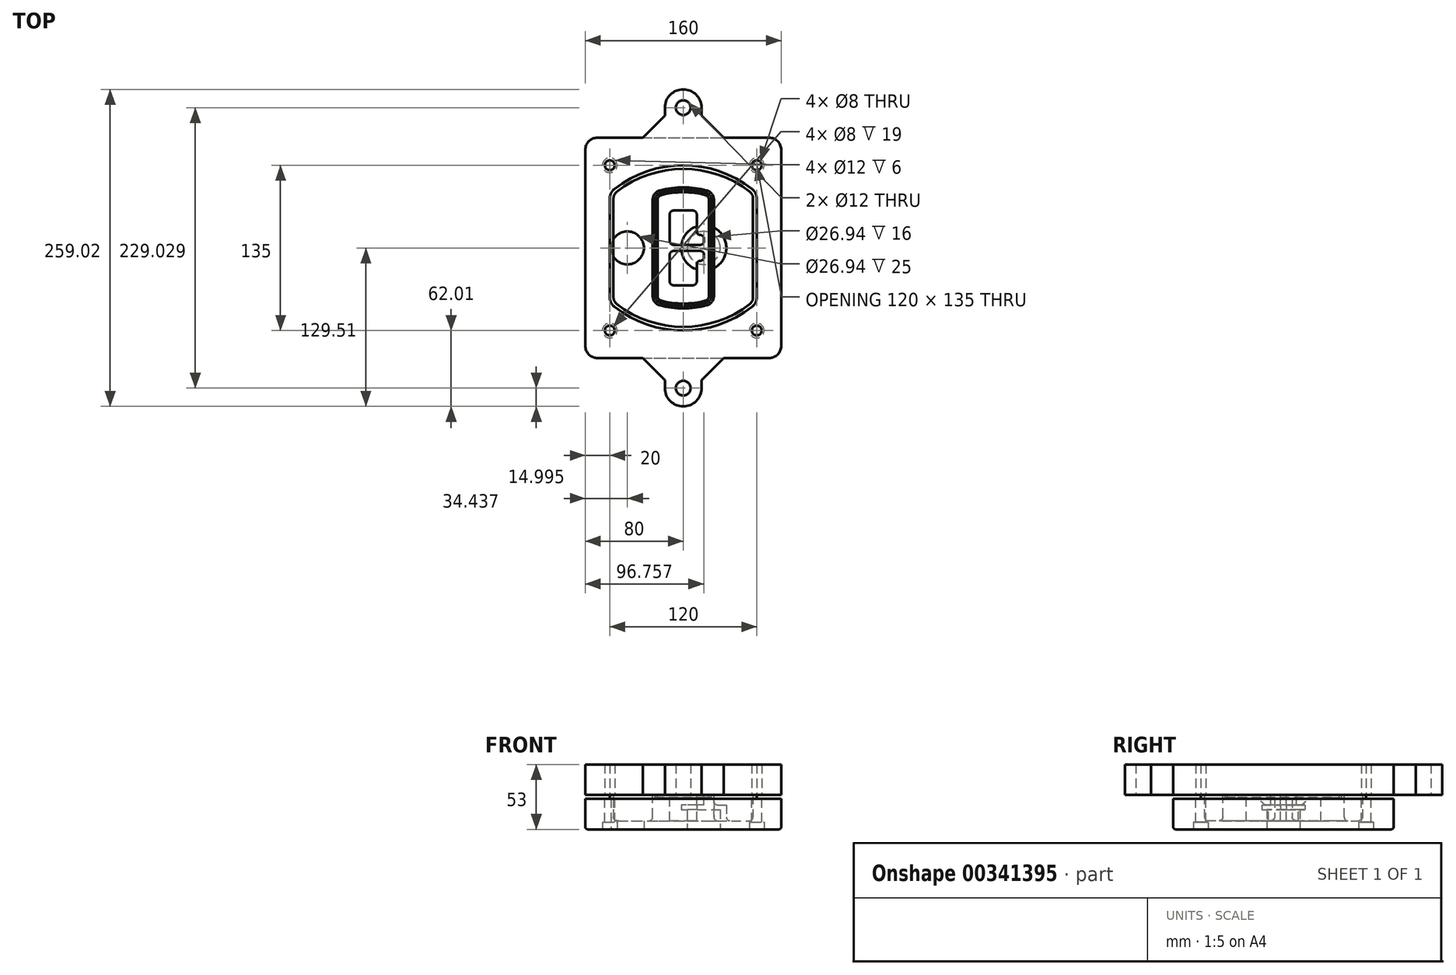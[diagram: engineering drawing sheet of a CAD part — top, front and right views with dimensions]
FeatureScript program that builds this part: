
annotation { "Feature Type Name" : "Feature", "Feature Type Description" : "" }
export const myFeature = defineFeature(function(context is Context, id is Id, definition is map)
    precondition{}
    {
        {
            var Q0;
            Q0=qCreatedBy(makeId("Top.planeOp"),FACE);
            var sketch = newSketch(context, id + "F0", { "sketchPlane" : qUnion([Q0])});
            skPoint(sketch, "E0.rect.middle", {"position": v(0, 0) * mm});
            skLineSegment(sketch, "E1.bottom", {"start": v(-70, -90) * mm, "end": v(70, -90) * mm});
            skLineSegment(sketch, "E1.top", {"start": v(-70, 90) * mm, "end": v(70, 90) * mm});
            skLineSegment(sketch, "E1.left", {"start": v(-80, -80) * mm, "end": v(-80, 80) * mm});
            skLineSegment(sketch, "E1.right", {"start": v(80, -80) * mm, "end": v(80, 80) * mm});
            skLineSegment(sketch, "E2", {"start": v(-80, 90) * mm, "end": v(80, -90) * mm, "construction": true});
            skLineSegment(sketch, "E3", {"start": v(80, 90) * mm, "end": v(-80, -90) * mm, "construction": true});
            skCircle(sketch, "E4", {"center": v(-60, 67.5) * mm, "radius": 4 * mm});
            skCircle(sketch, "E5", {"center": v(60, 67.5) * mm, "radius": 4 * mm});
            skCircle(sketch, "E6", {"center": v(60, -67.5) * mm, "radius": 4 * mm});
            skCircle(sketch, "E7", {"center": v(-60, -67.5) * mm, "radius": 4 * mm});
            skLineSegment(sketch, "E8", {"start": v(-60, 67.5) * mm, "end": v(60, 67.5) * mm, "construction": true});
            skLineSegment(sketch, "E9", {"start": v(60, 67.5) * mm, "end": v(60, -67.5) * mm, "construction": true});
            skLineSegment(sketch, "E10", {"start": v(60, -67.5) * mm, "end": v(-60, -67.5) * mm, "construction": true});
            skLineSegment(sketch, "E11", {"start": v(-60, -67.5) * mm, "end": v(-60, 67.5) * mm, "construction": true});
            skLineSegment(sketch, "E12", {"start": v(-60, 40.3) * mm, "end": v(-60, -40.3) * mm});
            skLineSegment(sketch, "E13", {"start": v(60, 40.3) * mm, "end": v(60, -40.3) * mm});
            skArc(sketch, "E14", {"start": v(56.15, 48.18) * mm, "mid": v(0, 67.5) * mm, "end": v(-56.15, 48.18) * mm});
            skArc(sketch, "E15", {"start": v(-56.15, -48.18) * mm, "mid": v(0, -67.5) * mm, "end": v(56.15, -48.18) * mm});
            skLineSegment(sketch, "E16", {"start": v(-60, 0) * mm, "end": v(60, 0) * mm, "construction": true});
            skPoint(sketch, "E17.visualSharp", {"position": v(-60, -45) * mm});
            skArc(sketch, "E17.filletArc", {"start": v(-60, -40.3) * mm, "mid": v(-58.99, -44.68) * mm, "end": v(-56.15, -48.18) * mm});
            skPoint(sketch, "E18.visualSharp", {"position": v(-60, 45) * mm});
            skArc(sketch, "E18.filletArc", {"start": v(-56.15, 48.18) * mm, "mid": v(-58.99, 44.68) * mm, "end": v(-60, 40.3) * mm});
            skPoint(sketch, "E19.visualSharp", {"position": v(60, 45) * mm});
            skArc(sketch, "E19.filletArc", {"start": v(60, 40.3) * mm, "mid": v(58.99, 44.68) * mm, "end": v(56.15, 48.18) * mm});
            skPoint(sketch, "E20.visualSharp", {"position": v(60, -45) * mm});
            skArc(sketch, "E20.filletArc", {"start": v(56.15, -48.18) * mm, "mid": v(58.99, -44.68) * mm, "end": v(60, -40.3) * mm});
            skPoint(sketch, "E21.visualSharp", {"position": v(-80, 90) * mm});
            skArc(sketch, "E21.filletArc", {"start": v(-70, 90) * mm, "mid": v(-77.07, 87.07) * mm, "end": v(-80, 80) * mm});
            skPoint(sketch, "E22.visualSharp", {"position": v(80, 90) * mm});
            skArc(sketch, "E22.filletArc", {"start": v(80, 80) * mm, "mid": v(77.07, 87.07) * mm, "end": v(70, 90) * mm});
            skPoint(sketch, "E23.visualSharp", {"position": v(80, -90) * mm});
            skArc(sketch, "E23.filletArc", {"start": v(70, -90) * mm, "mid": v(77.07, -87.07) * mm, "end": v(80, -80) * mm});
            skPoint(sketch, "E24.visualSharp", {"position": v(-80, -90) * mm});
            skArc(sketch, "E24.filletArc", {"start": v(-80, -80) * mm, "mid": v(-77.07, -87.07) * mm, "end": v(-70, -90) * mm});
            skArc(sketch, "E25.0", {"start": v(57, 40.3) * mm, "mid": v(56.3, 43.36) * mm, "end": v(54.3, 45.81) * mm});
            skLineSegment(sketch, "E25.1", {"start": v(57, 40.3) * mm, "end": v(57, -40.3) * mm});
            skArc(sketch, "E25.2", {"start": v(54.3, -45.81) * mm, "mid": v(56.3, -43.36) * mm, "end": v(57, -40.3) * mm});
            skArc(sketch, "E25.3", {"start": v(-54.3, -45.81) * mm, "mid": v(0, -64.5) * mm, "end": v(54.3, -45.81) * mm});
            skArc(sketch, "E25.4", {"start": v(-57, -40.3) * mm, "mid": v(-56.3, -43.36) * mm, "end": v(-54.3, -45.81) * mm});
            skArc(sketch, "E25.5", {"start": v(54.3, 45.81) * mm, "mid": v(0, 64.5) * mm, "end": v(-54.3, 45.81) * mm});
            skLineSegment(sketch, "E25.6", {"start": v(-57, 40.3) * mm, "end": v(-57, -40.3) * mm});
            skArc(sketch, "E25.7", {"start": v(-54.3, 45.81) * mm, "mid": v(-56.3, 43.36) * mm, "end": v(-57, 40.3) * mm});
            skArc(sketch, "E26.0", {"start": v(-58.62, 51.33) * mm, "mid": v(-62.58, 46.43) * mm, "end": v(-64, 40.3) * mm});
            skArc(sketch, "E26.1", {"start": v(58.62, 51.33) * mm, "mid": v(0, 71.5) * mm, "end": v(-58.62, 51.33) * mm});
            skArc(sketch, "E26.2", {"start": v(64, 40.3) * mm, "mid": v(62.58, 46.43) * mm, "end": v(58.62, 51.33) * mm});
            skLineSegment(sketch, "E26.3", {"start": v(64, 40.3) * mm, "end": v(64, -40.3) * mm});
            skArc(sketch, "E26.4", {"start": v(58.62, -51.33) * mm, "mid": v(62.58, -46.43) * mm, "end": v(64, -40.3) * mm});
            skLineSegment(sketch, "E26.5", {"start": v(-64, 40.3) * mm, "end": v(-64, -40.3) * mm});
            skArc(sketch, "E26.6", {"start": v(-58.62, -51.33) * mm, "mid": v(0, -71.5) * mm, "end": v(58.62, -51.33) * mm});
            skArc(sketch, "E26.7", {"start": v(-64, -40.3) * mm, "mid": v(-62.58, -46.43) * mm, "end": v(-58.62, -51.33) * mm});
            skSolve(sketch);
        }
        {
            var Q0;
            Q0=makeQuery(id+"F0.imprint","IMPRINT",FACE,{"disambiguationData":[TD([[makeQuery(id+"F0.imprint","IMPRINT",EDGE,{"derivedFrom":sQuery(id+"F0.wireOp",EDGE,"E1.bottom")}),1.0]])]});
            var Q1;
            Q1=makeQuery(id+"F0.imprint","IMPRINT",FACE,{"disambiguationData":[TD([[makeQuery(id+"F0.imprint","IMPRINT",EDGE,{"derivedFrom":sQuery(id+"F0.wireOp",EDGE,"E12")}),1.0]])]});
            var Q2;
            Q2=makeQuery(id+"F0.imprint","IMPRINT",FACE,{"disambiguationData":[TD([[makeQuery(id+"F0.imprint","IMPRINT",EDGE,{"derivedFrom":sQuery(id+"F0.wireOp",EDGE,"E25.0")}),1.0]])]});
            var Q3;
            Q3=makeQuery(id+"F0.imprint","IMPRINT",FACE,{"disambiguationData":[TD([[makeQuery(id+"F0.imprint","IMPRINT",EDGE,{"derivedFrom":sQuery(id+"F0.wireOp",EDGE,"E12")}),-1.0]])]});
            extrude(context, id + "F1", {"entities" : qUnion([Q0, Q1, Q2, Q3]), "oppositeDirection" : true, "depth" : 25 * mm});
        }
        {
            var Q0;
            Q0=makeQuery(id+"F0.imprint","IMPRINT",FACE,{"disambiguationData":[TD([[makeQuery(id+"F0.imprint","IMPRINT",EDGE,{"derivedFrom":sQuery(id+"F0.wireOp",EDGE,"E12")}),1.0]])]});
            extrude(context, id + "F2", {"entities" : qUnion([Q0]), "operationType" : NewBodyOperationType.ADD, "depth" : 3 * mm});
        }
        {
            var Q0;
            Q0=makeQuery(id+"F0.imprint","IMPRINT",FACE,{"disambiguationData":[TD([[makeQuery(id+"F0.imprint","IMPRINT",EDGE,{"derivedFrom":sQuery(id+"F0.wireOp",EDGE,"E25.0")}),1.0]])]});
            extrude(context, id + "F3", {"entities" : qUnion([Q0]), "operationType" : NewBodyOperationType.REMOVE, "oppositeDirection" : true, "depth" : 18 * mm});
        }
        {
            var Q0;
            Q0=makeQuery(id+"F2.opExtrude","CAP_FACE",FACE,{"disambiguationData":[OSD([sQuery(id+"F0.wireOp",EDGE,"E12"),sQuery(id+"F0.wireOp",EDGE,"E13"),sQuery(id+"F0.wireOp",EDGE,"E14"),sQuery(id+"F0.wireOp",EDGE,"E15"),sQuery(id+"F0.wireOp",EDGE,"E17.filletArc"),sQuery(id+"F0.wireOp",EDGE,"E18.filletArc"),sQuery(id+"F0.wireOp",EDGE,"E19.filletArc"),sQuery(id+"F0.wireOp",EDGE,"E20.filletArc"),sQuery(id+"F0.wireOp",EDGE,"E25.0"),sQuery(id+"F0.wireOp",EDGE,"E25.1"),sQuery(id+"F0.wireOp",EDGE,"E25.2"),sQuery(id+"F0.wireOp",EDGE,"E25.3"),sQuery(id+"F0.wireOp",EDGE,"E25.4"),sQuery(id+"F0.wireOp",EDGE,"E25.5"),sQuery(id+"F0.wireOp",EDGE,"E25.6"),sQuery(id+"F0.wireOp",EDGE,"E25.7")])],"isStart":false});
            var sketch = newSketch(context, id + "F4", { "sketchPlane" : qUnion([Q0])});
            skArc(sketch, "E27.0", {"start": v(-19.08, -46.97) * mm, "mid": v(0, -49.5) * mm, "end": v(19.08, -46.97) * mm});
            skArc(sketch, "E28.0", {"start": v(19.08, 46.97) * mm, "mid": v(0, 49.5) * mm, "end": v(-19.08, 46.97) * mm});
            skLineSegment(sketch, "E29", {"start": v(-25, 39.25) * mm, "end": v(-25, -39.25) * mm});
            skLineSegment(sketch, "E30", {"start": v(25, 39.25) * mm, "end": v(25, -39.25) * mm});
            skLineSegment(sketch, "E31", {"start": v(-25, 45.1) * mm, "end": v(25, 45.1) * mm, "construction": true});
            skLineSegment(sketch, "E32", {"start": v(-25, -45.1) * mm, "end": v(25, -45.1) * mm, "construction": true});
            skPoint(sketch, "E33.visualSharp", {"position": v(-25, 45.1) * mm});
            skArc(sketch, "E33.filletArc", {"start": v(-19.08, 46.97) * mm, "mid": v(-23.35, 44.11) * mm, "end": v(-25, 39.25) * mm});
            skPoint(sketch, "E34.visualSharp", {"position": v(25, 45.1) * mm});
            skArc(sketch, "E34.filletArc", {"start": v(25, 39.25) * mm, "mid": v(23.35, 44.11) * mm, "end": v(19.08, 46.97) * mm});
            skPoint(sketch, "E35.visualSharp", {"position": v(25, -45.1) * mm});
            skArc(sketch, "E35.filletArc", {"start": v(19.08, -46.97) * mm, "mid": v(23.35, -44.11) * mm, "end": v(25, -39.25) * mm});
            skPoint(sketch, "E36.visualSharp", {"position": v(-25, -45.1) * mm});
            skArc(sketch, "E36.filletArc", {"start": v(-25, -39.25) * mm, "mid": v(-23.35, -44.11) * mm, "end": v(-19.08, -46.97) * mm});
            skArc(sketch, "E37.0", {"start": v(54.3, 45.81) * mm, "mid": v(0, 64.5) * mm, "end": v(-54.3, 45.81) * mm});
            skArc(sketch, "E37.1", {"start": v(-54.3, 45.81) * mm, "mid": v(-56.3, 43.36) * mm, "end": v(-57, 40.3) * mm});
            skLineSegment(sketch, "E37.2", {"start": v(-57, 40.3) * mm, "end": v(-57, -40.3) * mm});
            skArc(sketch, "E37.3", {"start": v(-57, -40.3) * mm, "mid": v(-56.3, -43.36) * mm, "end": v(-54.3, -45.81) * mm});
            skArc(sketch, "E37.4", {"start": v(-54.3, -45.81) * mm, "mid": v(0, -64.5) * mm, "end": v(54.3, -45.81) * mm});
            skArc(sketch, "E37.5", {"start": v(54.3, -45.81) * mm, "mid": v(56.3, -43.36) * mm, "end": v(57, -40.3) * mm});
            skLineSegment(sketch, "E37.6", {"start": v(57, 40.3) * mm, "end": v(57, -40.3) * mm});
            skArc(sketch, "E37.7", {"start": v(57, 40.3) * mm, "mid": v(56.3, 43.36) * mm, "end": v(54.3, 45.81) * mm});
            skLineSegment(sketch, "E38.0", {"start": v(23, 39.25) * mm, "end": v(23, -39.25) * mm});
            skArc(sketch, "E38.1", {"start": v(18.56, -45.04) * mm, "mid": v(21.76, -42.9) * mm, "end": v(23, -39.25) * mm});
            skArc(sketch, "E38.2", {"start": v(-18.56, -45.04) * mm, "mid": v(0, -47.5) * mm, "end": v(18.56, -45.04) * mm});
            skArc(sketch, "E38.3", {"start": v(-23, -39.25) * mm, "mid": v(-21.76, -42.9) * mm, "end": v(-18.56, -45.04) * mm});
            skLineSegment(sketch, "E38.4", {"start": v(-23, 39.25) * mm, "end": v(-23, -39.25) * mm});
            skArc(sketch, "E38.5", {"start": v(23, 39.25) * mm, "mid": v(21.76, 42.9) * mm, "end": v(18.56, 45.04) * mm});
            skArc(sketch, "E38.6", {"start": v(-18.56, 45.04) * mm, "mid": v(-21.76, 42.9) * mm, "end": v(-23, 39.25) * mm});
            skArc(sketch, "E38.7", {"start": v(18.56, 45.04) * mm, "mid": v(0, 47.5) * mm, "end": v(-18.56, 45.04) * mm});
            skArc(sketch, "E39.0", {"start": v(21, 39.25) * mm, "mid": v(20.18, 41.68) * mm, "end": v(18.04, 43.1) * mm});
            skLineSegment(sketch, "E39.1", {"start": v(21, 39.25) * mm, "end": v(21, -39.25) * mm});
            skArc(sketch, "E39.2", {"start": v(18.04, -43.1) * mm, "mid": v(20.18, -41.68) * mm, "end": v(21, -39.25) * mm});
            skArc(sketch, "E39.3", {"start": v(-18.04, -43.1) * mm, "mid": v(0, -45.5) * mm, "end": v(18.04, -43.1) * mm});
            skArc(sketch, "E39.4", {"start": v(-21, -39.25) * mm, "mid": v(-20.18, -41.68) * mm, "end": v(-18.04, -43.1) * mm});
            skArc(sketch, "E39.5", {"start": v(18.04, 43.1) * mm, "mid": v(0, 45.5) * mm, "end": v(-18.04, 43.1) * mm});
            skLineSegment(sketch, "E39.6", {"start": v(-21, 39.25) * mm, "end": v(-21, -39.25) * mm});
            skArc(sketch, "E39.7", {"start": v(-18.04, 43.1) * mm, "mid": v(-20.18, 41.68) * mm, "end": v(-21, 39.25) * mm});
            skLineSegment(sketch, "E40", {"start": v(-25, 0) * mm, "end": v(25, 0) * mm, "construction": true});
            skLineSegment(sketch, "E41", {"start": v(-11, 5.5) * mm, "end": v(-11, 27.5) * mm});
            skLineSegment(sketch, "E42", {"start": v(-8, 30.5) * mm, "end": v(8, 30.5) * mm});
            skLineSegment(sketch, "E43", {"start": v(11, 27.5) * mm, "end": v(11, 13.5) * mm});
            skLineSegment(sketch, "E44", {"start": v(14, 10.5) * mm, "end": v(14, 10.5) * mm});
            skLineSegment(sketch, "E45", {"start": v(17, 7.5) * mm, "end": v(17, 5.5) * mm});
            skLineSegment(sketch, "E46", {"start": v(14, 2.5) * mm, "end": v(-8, 2.5) * mm});
            skPoint(sketch, "E47.visualSharp", {"position": v(-11, 30.5) * mm});
            skArc(sketch, "E47.filletArc", {"start": v(-8, 30.5) * mm, "mid": v(-10.12, 29.62) * mm, "end": v(-11, 27.5) * mm});
            skPoint(sketch, "E48.visualSharp", {"position": v(11, 30.5) * mm});
            skArc(sketch, "E48.filletArc", {"start": v(11, 27.5) * mm, "mid": v(10.12, 29.62) * mm, "end": v(8, 30.5) * mm});
            skPoint(sketch, "E49.visualSharp", {"position": v(11, 10.5) * mm});
            skArc(sketch, "E49.filletArc", {"start": v(11, 13.5) * mm, "mid": v(11.88, 11.38) * mm, "end": v(14, 10.5) * mm});
            skPoint(sketch, "E50.visualSharp", {"position": v(17, 10.5) * mm});
            skArc(sketch, "E50.filletArc", {"start": v(17, 7.5) * mm, "mid": v(16.12, 9.62) * mm, "end": v(14, 10.5) * mm});
            skPoint(sketch, "E51.visualSharp", {"position": v(17, 2.5) * mm});
            skArc(sketch, "E51.filletArc", {"start": v(14, 2.5) * mm, "mid": v(16.12, 3.38) * mm, "end": v(17, 5.5) * mm});
            skPoint(sketch, "E52.visualSharp", {"position": v(-11, 2.5) * mm});
            skArc(sketch, "E52.filletArc", {"start": v(-11, 5.5) * mm, "mid": v(-10.12, 3.38) * mm, "end": v(-8, 2.5) * mm});
            skLineSegment(sketch, "E53.0.MirrorCS", {"start": v(14, -2.5) * mm, "end": v(-8, -2.5) * mm});
            skArc(sketch, "E54.0.MirrorCS", {"start": v(-11, -5.5) * mm, "mid": v(-10.12, -3.38) * mm, "end": v(-8, -2.5) * mm});
            skLineSegment(sketch, "E55.0.MirrorCS", {"start": v(-11, -5.5) * mm, "end": v(-11, -27.5) * mm});
            skArc(sketch, "E56.0.MirrorCS", {"start": v(-8, -30.5) * mm, "mid": v(-10.12, -29.62) * mm, "end": v(-11, -27.5) * mm});
            skLineSegment(sketch, "E57.0.MirrorCS", {"start": v(-8, -30.5) * mm, "end": v(8, -30.5) * mm});
            skArc(sketch, "E58.0.MirrorCS", {"start": v(11, -27.5) * mm, "mid": v(10.12, -29.62) * mm, "end": v(8, -30.5) * mm});
            skLineSegment(sketch, "E59.0.MirrorCS", {"start": v(11, -27.5) * mm, "end": v(11, -13.5) * mm});
            skArc(sketch, "E60.0.MirrorCS", {"start": v(11, -13.5) * mm, "mid": v(11.88, -11.38) * mm, "end": v(14, -10.5) * mm});
            skArc(sketch, "E61.0.MirrorCS", {"start": v(17, -7.5) * mm, "mid": v(16.12, -9.62) * mm, "end": v(14, -10.5) * mm});
            skLineSegment(sketch, "E62.0.MirrorCS", {"start": v(17, -7.5) * mm, "end": v(17, -5.5) * mm});
            skArc(sketch, "E63.0.MirrorCS", {"start": v(14, -2.5) * mm, "mid": v(16.12, -3.38) * mm, "end": v(17, -5.5) * mm});
            skSolve(sketch);
        }
        {
            var Q0;
            Q0=makeQuery(id+"F4.imprint","IMPRINT",FACE,{"disambiguationData":[TD([[makeQuery(id+"F4.imprint","IMPRINT",EDGE,{"derivedFrom":sQuery(id+"F4.wireOp",EDGE,"E27.0")}),1.0]])]});
            var Q1;
            Q1=makeQuery(id+"F4.imprint","IMPRINT",FACE,{"disambiguationData":[TD([[makeQuery(id+"F4.imprint","IMPRINT",EDGE,{"derivedFrom":sQuery(id+"F4.wireOp",EDGE,"E38.0")}),-1.0]])]});
            var Q2;
            Q2=makeQuery(id+"F4.imprint","IMPRINT",FACE,{"disambiguationData":[TD([[makeQuery(id+"F4.imprint","IMPRINT",EDGE,{"derivedFrom":sQuery(id+"F4.wireOp",EDGE,"E39.0")}),1.0]])]});
            extrude(context, id + "F5", {"entities" : qUnion([Q0, Q1, Q2]), "operationType" : NewBodyOperationType.ADD, "endBound" : BoundingType.UP_TO_NEXT, "oppositeDirection" : true, "depth" : 25 * mm});
        }
        {
            var Q0;
            Q0=makeQuery(id+"F4.imprint","IMPRINT",FACE,{"disambiguationData":[TD([[makeQuery(id+"F4.imprint","IMPRINT",EDGE,{"derivedFrom":sQuery(id+"F4.wireOp",EDGE,"E38.0")}),-1.0]])]});
            extrude(context, id + "F6", {"entities" : qUnion([Q0]), "operationType" : NewBodyOperationType.REMOVE, "oppositeDirection" : true, "depth" : 2 * mm});
        }
        {
            var Q0;
            Q0=makeQuery(id+"F1.opExtrude","CAP_FACE",FACE,{"disambiguationData":[OSD([sQuery(id+"F0.wireOp",EDGE,"E1.bottom"),sQuery(id+"F0.wireOp",EDGE,"E1.top"),sQuery(id+"F0.wireOp",EDGE,"E1.left"),sQuery(id+"F0.wireOp",EDGE,"E1.right"),sQuery(id+"F0.wireOp",EDGE,"E4"),sQuery(id+"F0.wireOp",EDGE,"E5"),sQuery(id+"F0.wireOp",EDGE,"E6"),sQuery(id+"F0.wireOp",EDGE,"E7"),sQuery(id+"F0.wireOp",EDGE,"E21.filletArc"),sQuery(id+"F0.wireOp",EDGE,"E22.filletArc"),sQuery(id+"F0.wireOp",EDGE,"E23.filletArc"),sQuery(id+"F0.wireOp",EDGE,"E24.filletArc")])],"isStart":false});
            var sketch = newSketch(context, id + "F7", { "sketchPlane" : qUnion([Q0])});
            skCircle(sketch, "E64", {"center": v(16.76, 0) * mm, "radius": 13.47 * mm});
            skCircle(sketch, "E65", {"center": v(-45.56, 0) * mm, "radius": 13.47 * mm});
            skLineSegment(sketch, "E66", {"start": v(80, 0) * mm, "end": v(-80, 0) * mm});
            skCircle(sketch, "E67", {"center": v(16.76, 0) * mm, "radius": 18.47 * mm});
            skCircle(sketch, "E68", {"center": v(60, -67.5) * mm, "radius": 6 * mm});
            skCircle(sketch, "E69", {"center": v(-60, -67.5) * mm, "radius": 6 * mm});
            skCircle(sketch, "E70", {"center": v(-60, 67.5) * mm, "radius": 6 * mm});
            skCircle(sketch, "E71", {"center": v(60, 67.5) * mm, "radius": 6 * mm});
            skSolve(sketch);
        }
        {
            var Q0;
            {var subQ1=sQuery(id+"F7.wireOp",EDGE,"E66");var subQ4=sQuery(id+"F7.wireOp",EDGE,"E64");var subQ6=makeQuery(id+"F7.imprint","INTERSECT",VERTEX,{"disambiguationData":[OD(0.0)],"derivedFrom":[subQ4,subQ1]});Q0=makeQuery(id+"F7.imprint","IMPRINT",FACE,{"disambiguationData":[TD([[makeQuery(id+"F7.imprint","IMPRINT",EDGE,{"disambiguationData":[TD([[subQ6,-1.0]])],"derivedFrom":subQ4}),-1.0]])]});}
            var Q1;
            {var subQ0=sQuery(id+"F7.wireOp",EDGE,"E66");var subQ1=sQuery(id+"F7.wireOp",EDGE,"E64");var subQ3=makeQuery(id+"F7.imprint","INTERSECT",VERTEX,{"disambiguationData":[OD(0.0)],"derivedFrom":[subQ1,subQ0]});Q1=makeQuery(id+"F7.imprint","IMPRINT",FACE,{"disambiguationData":[TD([[makeQuery(id+"F7.imprint","IMPRINT",EDGE,{"disambiguationData":[TD([[subQ3,-1.0]])],"derivedFrom":subQ1}),1.0]])]});}
            var Q2;
            {var subQ0=sQuery(id+"F7.wireOp",EDGE,"E66");var subQ1=sQuery(id+"F7.wireOp",EDGE,"E64");var subQ3=makeQuery(id+"F7.imprint","INTERSECT",VERTEX,{"disambiguationData":[OD(0.0)],"derivedFrom":[subQ1,subQ0]});Q2=makeQuery(id+"F7.imprint","IMPRINT",FACE,{"disambiguationData":[TD([[makeQuery(id+"F7.imprint","IMPRINT",EDGE,{"disambiguationData":[TD([[subQ3,1.0]])],"derivedFrom":subQ1}),1.0]])]});}
            var Q3;
            {var subQ1=sQuery(id+"F7.wireOp",EDGE,"E66");var subQ4=sQuery(id+"F7.wireOp",EDGE,"E64");var subQ6=makeQuery(id+"F7.imprint","INTERSECT",VERTEX,{"disambiguationData":[OD(0.0)],"derivedFrom":[subQ4,subQ1]});Q3=makeQuery(id+"F7.imprint","IMPRINT",FACE,{"disambiguationData":[TD([[makeQuery(id+"F7.imprint","IMPRINT",EDGE,{"disambiguationData":[TD([[subQ6,1.0]])],"derivedFrom":subQ4}),-1.0]])]});}
            extrude(context, id + "F8", {"entities" : qUnion([Q0, Q1, Q2, Q3]), "operationType" : NewBodyOperationType.ADD, "oppositeDirection" : true, "depth" : 20 * mm});
        }
        {
            var Q0;
            {var subQ0=sQuery(id+"F7.wireOp",EDGE,"E66");var subQ1=sQuery(id+"F7.wireOp",EDGE,"E64");var subQ3=makeQuery(id+"F7.imprint","INTERSECT",VERTEX,{"disambiguationData":[OD(0.0)],"derivedFrom":[subQ1,subQ0]});Q0=makeQuery(id+"F7.imprint","IMPRINT",FACE,{"disambiguationData":[TD([[makeQuery(id+"F7.imprint","IMPRINT",EDGE,{"disambiguationData":[TD([[subQ3,-1.0]])],"derivedFrom":subQ1}),1.0]])]});}
            var Q1;
            {var subQ0=sQuery(id+"F7.wireOp",EDGE,"E66");var subQ1=sQuery(id+"F7.wireOp",EDGE,"E64");var subQ3=makeQuery(id+"F7.imprint","INTERSECT",VERTEX,{"disambiguationData":[OD(0.0)],"derivedFrom":[subQ1,subQ0]});Q1=makeQuery(id+"F7.imprint","IMPRINT",FACE,{"disambiguationData":[TD([[makeQuery(id+"F7.imprint","IMPRINT",EDGE,{"disambiguationData":[TD([[subQ3,1.0]])],"derivedFrom":subQ1}),1.0]])]});}
            extrude(context, id + "F9", {"entities" : qUnion([Q0, Q1]), "operationType" : NewBodyOperationType.REMOVE, "oppositeDirection" : true, "depth" : 16 * mm});
        }
        {
            var Q0;
            {var subQ0=sQuery(id+"F7.wireOp",EDGE,"E66");var subQ1=sQuery(id+"F7.wireOp",EDGE,"E65");var subQ3=makeQuery(id+"F7.imprint","INTERSECT",VERTEX,{"disambiguationData":[OD(0.0)],"derivedFrom":[subQ1,subQ0]});Q0=makeQuery(id+"F7.imprint","IMPRINT",FACE,{"disambiguationData":[TD([[makeQuery(id+"F7.imprint","IMPRINT",EDGE,{"disambiguationData":[TD([[subQ3,-1.0]])],"derivedFrom":subQ1}),1.0]])]});}
            var Q1;
            {var subQ0=sQuery(id+"F7.wireOp",EDGE,"E66");var subQ1=sQuery(id+"F7.wireOp",EDGE,"E65");var subQ3=makeQuery(id+"F7.imprint","INTERSECT",VERTEX,{"disambiguationData":[OD(0.0)],"derivedFrom":[subQ1,subQ0]});Q1=makeQuery(id+"F7.imprint","IMPRINT",FACE,{"disambiguationData":[TD([[makeQuery(id+"F7.imprint","IMPRINT",EDGE,{"disambiguationData":[TD([[subQ3,1.0]])],"derivedFrom":subQ1}),1.0]])]});}
            extrude(context, id + "F10", {"entities" : qUnion([Q0, Q1]), "operationType" : NewBodyOperationType.REMOVE, "oppositeDirection" : true, "depth" : 25 * mm});
        }
        {
            var Q0;
            Q0=makeQuery(id+"F7.imprint","IMPRINT",FACE,{"disambiguationData":[TD([[makeQuery(id+"F7.imprint","IMPRINT",EDGE,{"derivedFrom":sQuery(id+"F7.wireOp",EDGE,"E68")}),1.0]])]});
            var Q1;
            Q1=makeQuery(id+"F7.imprint","IMPRINT",FACE,{"disambiguationData":[TD([[makeQuery(id+"F7.imprint","IMPRINT",EDGE,{"derivedFrom":makeQuery(id+"F1.opExtrude","CAP_EDGE",EDGE,{"disambiguationData":[OSD([sQuery(id+"F0.wireOp",EDGE,"E5")])],"isStart":false})}),-1.0]])]});
            var Q2;
            Q2=makeQuery(id+"F7.imprint","IMPRINT",FACE,{"disambiguationData":[TD([[makeQuery(id+"F7.imprint","IMPRINT",EDGE,{"derivedFrom":sQuery(id+"F7.wireOp",EDGE,"E69")}),1.0]])]});
            var Q3;
            Q3=makeQuery(id+"F7.imprint","IMPRINT",FACE,{"disambiguationData":[TD([[makeQuery(id+"F7.imprint","IMPRINT",EDGE,{"derivedFrom":makeQuery(id+"F1.opExtrude","CAP_EDGE",EDGE,{"disambiguationData":[OSD([sQuery(id+"F0.wireOp",EDGE,"E4")])],"isStart":false})}),-1.0]])]});
            var Q4;
            Q4=makeQuery(id+"F7.imprint","IMPRINT",FACE,{"disambiguationData":[TD([[makeQuery(id+"F7.imprint","IMPRINT",EDGE,{"derivedFrom":sQuery(id+"F7.wireOp",EDGE,"E70")}),1.0]])]});
            var Q5;
            Q5=makeQuery(id+"F7.imprint","IMPRINT",FACE,{"disambiguationData":[TD([[makeQuery(id+"F7.imprint","IMPRINT",EDGE,{"derivedFrom":makeQuery(id+"F1.opExtrude","CAP_EDGE",EDGE,{"disambiguationData":[OSD([sQuery(id+"F0.wireOp",EDGE,"E7")])],"isStart":false})}),-1.0]])]});
            var Q6;
            Q6=makeQuery(id+"F7.imprint","IMPRINT",FACE,{"disambiguationData":[TD([[makeQuery(id+"F7.imprint","IMPRINT",EDGE,{"derivedFrom":sQuery(id+"F7.wireOp",EDGE,"E71")}),1.0]])]});
            var Q7;
            Q7=makeQuery(id+"F7.imprint","IMPRINT",FACE,{"disambiguationData":[TD([[makeQuery(id+"F7.imprint","IMPRINT",EDGE,{"derivedFrom":makeQuery(id+"F1.opExtrude","CAP_EDGE",EDGE,{"disambiguationData":[OSD([sQuery(id+"F0.wireOp",EDGE,"E6")])],"isStart":false})}),-1.0]])]});
            extrude(context, id + "F11", {"entities" : qUnion([Q0, Q1, Q2, Q3, Q4, Q5, Q6, Q7]), "operationType" : NewBodyOperationType.REMOVE, "oppositeDirection" : true, "depth" : 6 * mm});
        }
        {
            var Q0;
            Q0=makeQuery(id+"F9.boolean.opBoolean","COPY",FACE,{"derivedFrom":makeQuery(id+"F9.opExtrude","CAP_FACE",FACE,{"disambiguationData":[OSD([sQuery(id+"F7.wireOp",EDGE,"E64")])],"isStart":false})});
            var sketch = newSketch(context, id + "F12", { "sketchPlane" : qUnion([Q0])});
            skArc(sketch, "E72.0", {"start": v(11, 17.55) * mm, "mid": v(2.57, 11.82) * mm, "end": v(-1.54, 2.5) * mm});
            skArc(sketch, "E72.1", {"start": v(-1.54, -2.5) * mm, "mid": v(2.57, -11.82) * mm, "end": v(11, -17.55) * mm});
            skLineSegment(sketch, "E73", {"start": v(-1.54, -2.5) * mm, "end": v(14, -2.5) * mm});
            skLineSegment(sketch, "E74.0", {"start": v(14, 2.5) * mm, "end": v(-1.54, 2.5) * mm});
            skArc(sketch, "E74.1", {"start": v(14, 2.5) * mm, "mid": v(16.12, 3.38) * mm, "end": v(17, 5.5) * mm});
            skLineSegment(sketch, "E74.2", {"start": v(17, 7.5) * mm, "end": v(17, 5.5) * mm});
            skArc(sketch, "E74.3", {"start": v(17, 7.5) * mm, "mid": v(16.12, 9.62) * mm, "end": v(14, 10.5) * mm});
            skArc(sketch, "E74.4", {"start": v(11, 13.5) * mm, "mid": v(11.88, 11.38) * mm, "end": v(14, 10.5) * mm});
            skLineSegment(sketch, "E74.5", {"start": v(11, 17.55) * mm, "end": v(11, 13.5) * mm});
            skLineSegment(sketch, "E74.7", {"start": v(14, -2.5) * mm, "end": v(-1.54, -2.5) * mm});
            skArc(sketch, "E74.8", {"start": v(14, -2.5) * mm, "mid": v(16.12, -3.38) * mm, "end": v(17, -5.5) * mm});
            skLineSegment(sketch, "E74.9", {"start": v(17, -7.5) * mm, "end": v(17, -5.5) * mm});
            skArc(sketch, "E74.10", {"start": v(17, -7.5) * mm, "mid": v(16.12, -9.62) * mm, "end": v(14, -10.5) * mm});
            skArc(sketch, "E74.11", {"start": v(11, -13.5) * mm, "mid": v(11.88, -11.38) * mm, "end": v(14, -10.5) * mm});
            skLineSegment(sketch, "E74.12", {"start": v(11, -17.55) * mm, "end": v(11, -13.5) * mm});
            skPoint(sketch, "E75.orphan", {"position": v(11, -27.5) * mm});
            skPoint(sketch, "E76.orphan", {"position": v(-8, -2.5) * mm});
            skPoint(sketch, "E77.orphan", {"position": v(-8, 2.5) * mm});
            skPoint(sketch, "E78.orphan", {"position": v(11, 27.5) * mm});
            skSolve(sketch);
        }
        {
            var Q0;
            {var subQ7=sQuery(id+"F12.wireOp",EDGE,"E72.0");var subQ14=sQuery(id+"F12.wireOp",EDGE,"E72.1");var subQ16=sQuery(id+"F12.wireOp",EDGE,"E74.1");var subQ18=sQuery(id+"F12.wireOp",EDGE,"E74.8");Q0=qUnion([makeQuery(id+"F12.imprint","IMPRINT",FACE,{"disambiguationData":[TD([[makeQuery(id+"F12.imprint","IMPRINT",EDGE,{"derivedFrom":subQ7}),1.0]])]}),makeQuery(id+"F12.imprint","IMPRINT",FACE,{"disambiguationData":[TD([[makeQuery(id+"F12.imprint","IMPRINT",EDGE,{"derivedFrom":subQ14}),1.0]])]}),makeQuery(id+"F12.imprint","IMPRINT",FACE,{"disambiguationData":[TD([[makeQuery(id+"F12.imprint","IMPRINT",EDGE,{"derivedFrom":subQ16}),1.0]])]}),makeQuery(id+"F12.imprint","IMPRINT",FACE,{"disambiguationData":[TD([[makeQuery(id+"F12.imprint","IMPRINT",EDGE,{"derivedFrom":subQ18}),-1.0]])]})]);}
            var Q1;
            Q1=makeQuery(id+"F5.boolean.opBoolean","SPLIT",FACE,{"disambiguationData":[TD([makeQuery(id+"F5.opExtrude","SWEPT_FACE",FACE,{"disambiguationData":[OSD([sQuery(id+"F4.wireOp",EDGE,"E41")])]})])],"derivedFrom":makeQuery(id+"F3.boolean.opBoolean","COPY",FACE,{"derivedFrom":makeQuery(id+"F3.opExtrude","CAP_FACE",FACE,{"disambiguationData":[OSD([sQuery(id+"F0.wireOp",EDGE,"E25.0"),sQuery(id+"F0.wireOp",EDGE,"E25.1"),sQuery(id+"F0.wireOp",EDGE,"E25.2"),sQuery(id+"F0.wireOp",EDGE,"E25.3"),sQuery(id+"F0.wireOp",EDGE,"E25.4"),sQuery(id+"F0.wireOp",EDGE,"E25.5"),sQuery(id+"F0.wireOp",EDGE,"E25.6"),sQuery(id+"F0.wireOp",EDGE,"E25.7")])],"isStart":false})})});
            extrude(context, id + "F13", {"entities" : qUnion([Q0]), "operationType" : NewBodyOperationType.REMOVE, "endBound" : BoundingType.UP_TO_SURFACE, "endBoundEntityFace" : qUnion([Q1]), "depth" : 25 * mm});
        }
        {
            var Q0;
            Q0=makeQuery(id+"F3.boolean.opBoolean","COPY",EDGE,{"derivedFrom":makeQuery(id+"F3.opExtrude","CAP_EDGE",EDGE,{"disambiguationData":[OSD([sQuery(id+"F0.wireOp",EDGE,"E25.6")])],"isStart":false})});
            var Q1;
            Q1=makeQuery(id+"F8.boolean.opBoolean","INTERSECT",EDGE,{"derivedFrom":[makeQuery(id+"F5.opExtrude","SWEPT_FACE",FACE,{"disambiguationData":[OSD([sQuery(id+"F4.wireOp",EDGE,"E30")])]}),makeQuery(id+"F8.opExtrude","CAP_FACE",FACE,{"disambiguationData":[OSD([sQuery(id+"F7.wireOp",EDGE,"E67")])],"isStart":false})]});
            var Q2;
            Q2=makeQuery(id+"F8.boolean.opBoolean","INTERSECT",EDGE,{"disambiguationData":[OD(1.0)],"derivedFrom":[makeQuery(id+"F5.opExtrude","SWEPT_FACE",FACE,{"disambiguationData":[OSD([sQuery(id+"F4.wireOp",EDGE,"E30")])]}),makeQuery(id+"F8.opExtrude","SWEPT_FACE",FACE,{"disambiguationData":[OSD([sQuery(id+"F7.wireOp",EDGE,"E67")])]})]});
            var Q3;
            {var subQ0=sQuery(id+"F4.wireOp",EDGE,"E30");Q3=makeQuery(id+"F8.boolean.opBoolean","SPLIT",EDGE,{"disambiguationData":[TD([makeQuery(id+"F5.opExtrude","SWEPT_FACE",FACE,{"disambiguationData":[OSD([sQuery(id+"F4.wireOp",EDGE,"E35.filletArc")])]})])],"derivedFrom":makeQuery(id+"F5.opExtrude","CAP_EDGE",EDGE,{"disambiguationData":[OSD([subQ0])],"isStart":false})});}
            var Q4;
            {var subQ0=sQuery(id+"F0.wireOp",EDGE,"E25.7");var subQ1=sQuery(id+"F0.wireOp",EDGE,"E25.1");var subQ2=sQuery(id+"F0.wireOp",EDGE,"E25.6");var subQ3=sQuery(id+"F0.wireOp",EDGE,"E25.5");var subQ4=sQuery(id+"F0.wireOp",EDGE,"E25.4");var subQ5=sQuery(id+"F0.wireOp",EDGE,"E25.0");var subQ6=sQuery(id+"F0.wireOp",EDGE,"E25.2");var subQ7=sQuery(id+"F0.wireOp",EDGE,"E25.3");Q4=makeQuery(id+"F8.boolean.opBoolean","INTERSECT",EDGE,{"derivedFrom":[makeQuery(id+"F5.boolean.opBoolean","SPLIT",FACE,{"disambiguationData":[TD([makeQuery(id+"F2.opExtrude","SWEPT_FACE",FACE,{"disambiguationData":[OSD([subQ5])]})])],"derivedFrom":makeQuery(id+"F3.boolean.opBoolean","COPY",FACE,{"derivedFrom":makeQuery(id+"F3.opExtrude","CAP_FACE",FACE,{"disambiguationData":[OSD([subQ5,subQ1,subQ6,subQ7,subQ4,subQ3,subQ2,subQ0])],"isStart":false})})}),makeQuery(id+"F8.opExtrude","SWEPT_FACE",FACE,{"disambiguationData":[OSD([sQuery(id+"F7.wireOp",EDGE,"E67")])]})]});}
            var Q5;
            Q5=makeQuery(id+"F8.boolean.opBoolean","INTERSECT",EDGE,{"disambiguationData":[OD(0.0)],"derivedFrom":[makeQuery(id+"F5.opExtrude","SWEPT_FACE",FACE,{"disambiguationData":[OSD([sQuery(id+"F4.wireOp",EDGE,"E30")])]}),makeQuery(id+"F8.opExtrude","SWEPT_FACE",FACE,{"disambiguationData":[OSD([sQuery(id+"F7.wireOp",EDGE,"E67")])]})]});
            fillet(context, id + "F14", {"entities" : qUnion([Q0, Q1, Q2, Q3, Q4, Q5]), "radius" : 3 * mm, "tangentPropagation" : true, "allowEdgeOverflow" : false});
        }
        {
            var Q0;
            Q0=makeQuery(id+"F1.opExtrude","CAP_EDGE",EDGE,{"disambiguationData":[OSD([sQuery(id+"F0.wireOp",EDGE,"E1.bottom")])],"isStart":false});
            fillet(context, id + "F15", {"entities" : qUnion([Q0]), "radius" : 2 * mm, "tangentPropagation" : true, "allowEdgeOverflow" : false});
        }
        {
            var Q0;
            Q0=makeQuery(id+"F2.opExtrude","CAP_FACE",FACE,{"disambiguationData":[OSD([sQuery(id+"F0.wireOp",EDGE,"E12"),sQuery(id+"F0.wireOp",EDGE,"E13"),sQuery(id+"F0.wireOp",EDGE,"E14"),sQuery(id+"F0.wireOp",EDGE,"E15"),sQuery(id+"F0.wireOp",EDGE,"E17.filletArc"),sQuery(id+"F0.wireOp",EDGE,"E18.filletArc"),sQuery(id+"F0.wireOp",EDGE,"E19.filletArc"),sQuery(id+"F0.wireOp",EDGE,"E20.filletArc"),sQuery(id+"F0.wireOp",EDGE,"E25.0"),sQuery(id+"F0.wireOp",EDGE,"E25.1"),sQuery(id+"F0.wireOp",EDGE,"E25.2"),sQuery(id+"F0.wireOp",EDGE,"E25.3"),sQuery(id+"F0.wireOp",EDGE,"E25.4"),sQuery(id+"F0.wireOp",EDGE,"E25.5"),sQuery(id+"F0.wireOp",EDGE,"E25.6"),sQuery(id+"F0.wireOp",EDGE,"E25.7")])],"isStart":false});
            var sketch = newSketch(context, id + "F16", { "sketchPlane" : qUnion([Q0])});
            skLineSegment(sketch, "E79.0", {"start": v(-70, 90) * mm, "end": v(70, 90) * mm});
            skArc(sketch, "E79.1", {"start": v(80, 80) * mm, "mid": v(77.07, 87.07) * mm, "end": v(70, 90) * mm});
            skLineSegment(sketch, "E79.2", {"start": v(80, -80) * mm, "end": v(80, 80) * mm});
            skLineSegment(sketch, "E79.3", {"start": v(-80, -80) * mm, "end": v(-80, 80) * mm});
            skArc(sketch, "E79.4", {"start": v(-70, 90) * mm, "mid": v(-77.07, 87.07) * mm, "end": v(-80, 80) * mm});
            skArc(sketch, "E79.5", {"start": v(-80, -80) * mm, "mid": v(-77.07, -87.07) * mm, "end": v(-70, -90) * mm});
            skLineSegment(sketch, "E79.6", {"start": v(-70, -90) * mm, "end": v(70, -90) * mm});
            skArc(sketch, "E79.7", {"start": v(70, -90) * mm, "mid": v(77.07, -87.07) * mm, "end": v(80, -80) * mm});
            skLineSegment(sketch, "E79.8", {"start": v(60, 40.3) * mm, "end": v(60, -40.3) * mm});
            skArc(sketch, "E79.9", {"start": v(56.15, -48.18) * mm, "mid": v(58.99, -44.68) * mm, "end": v(60, -40.3) * mm});
            skArc(sketch, "E79.10", {"start": v(-56.15, -48.18) * mm, "mid": v(0, -67.5) * mm, "end": v(56.15, -48.18) * mm});
            skArc(sketch, "E79.11", {"start": v(-60, -40.3) * mm, "mid": v(-58.99, -44.68) * mm, "end": v(-56.15, -48.18) * mm});
            skLineSegment(sketch, "E79.12", {"start": v(-60, 40.3) * mm, "end": v(-60, -40.3) * mm});
            skArc(sketch, "E79.13", {"start": v(-56.15, 48.18) * mm, "mid": v(-58.99, 44.68) * mm, "end": v(-60, 40.3) * mm});
            skArc(sketch, "E79.14", {"start": v(56.15, 48.18) * mm, "mid": v(0, 67.5) * mm, "end": v(-56.15, 48.18) * mm});
            skArc(sketch, "E79.15", {"start": v(60, 40.3) * mm, "mid": v(58.99, 44.68) * mm, "end": v(56.15, 48.18) * mm});
            skCircle(sketch, "E79.16", {"center": v(60, 67.5) * mm, "radius": 4 * mm});
            skCircle(sketch, "E79.17", {"center": v(-60, 67.5) * mm, "radius": 4 * mm});
            skCircle(sketch, "E79.18", {"center": v(-60, -67.5) * mm, "radius": 4 * mm});
            skCircle(sketch, "E79.19", {"center": v(60, -67.5) * mm, "radius": 4 * mm});
            skCircle(sketch, "E80", {"center": v(0, 114.51) * mm, "radius": 6 * mm});
            skLineSegment(sketch, "E81", {"start": v(0, 114.51) * mm, "end": v(0, 90) * mm, "construction": true});
            skArc(sketch, "E82", {"start": v(-15, 114.51) * mm, "mid": v(0, 129.51) * mm, "end": v(15, 114.51) * mm});
            skLineSegment(sketch, "E83", {"start": v(15, 114.51) * mm, "end": v(15, 108) * mm});
            skLineSegment(sketch, "E84", {"start": v(15, 108) * mm, "end": v(33, 90) * mm});
            skLineSegment(sketch, "E85", {"start": v(-15, 114.51) * mm, "end": v(-15, 108) * mm});
            skLineSegment(sketch, "E86", {"start": v(-15, 108) * mm, "end": v(-33, 90) * mm});
            skLineSegment(sketch, "E87", {"start": v(-80, 0) * mm, "end": v(80, 0) * mm, "construction": true});
            skLineSegment(sketch, "E88.MirrorCS", {"start": v(15, -108) * mm, "end": v(33, -90) * mm});
            skLineSegment(sketch, "E89.MirrorCS", {"start": v(-15, -114.51) * mm, "end": v(-15, -108) * mm});
            skLineSegment(sketch, "E90.MirrorCS", {"start": v(15, -114.51) * mm, "end": v(15, -108) * mm});
            skArc(sketch, "E91.MirrorCS", {"start": v(-15, -114.51) * mm, "mid": v(0, -129.51) * mm, "end": v(15, -114.51) * mm});
            skLineSegment(sketch, "E92.MirrorCS", {"start": v(-15, -108) * mm, "end": v(-33, -90) * mm});
            skCircle(sketch, "E93", {"center": v(0, -114.51) * mm, "radius": 6 * mm});
            skSolve(sketch);
        }
        {
            var Q0;
            Q0 = qSketchRegion(id + "F16", true);
            extrude(context, id + "F17", {"entities" : qUnion([Q0]), "depth" : 25 * mm});
        }
    });
